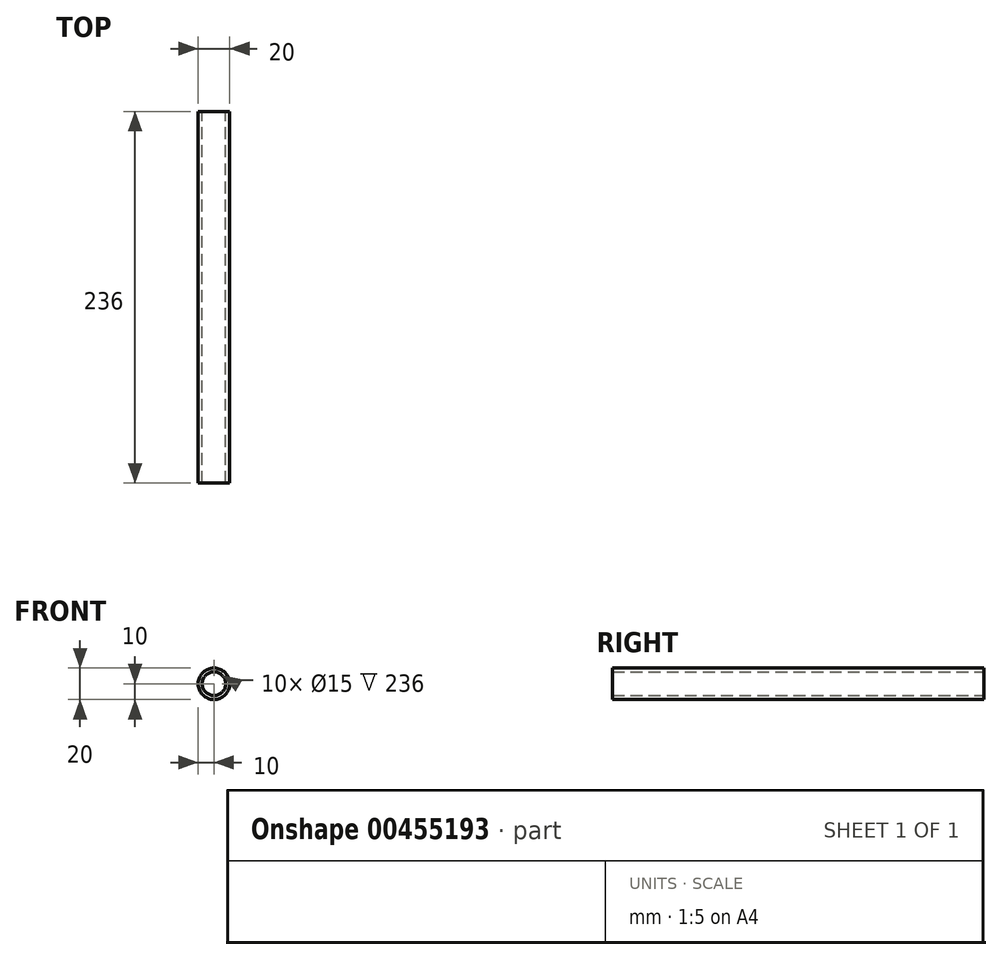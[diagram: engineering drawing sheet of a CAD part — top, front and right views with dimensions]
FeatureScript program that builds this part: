
annotation { "Feature Type Name" : "Feature", "Feature Type Description" : "" }
export const myFeature = defineFeature(function(context is Context, id is Id, definition is map)
    precondition{}
    {
        {
            var Q0;
            Q0=qCreatedBy(makeId("Front.planeOp"),FACE);
            var sketch = newSketch(context, id + "F0", { "sketchPlane" : qUnion([Q0])});
            skCircle(sketch, "E0", {"center": v(0, 0) * mm, "radius": 10 * mm});
            skCircle(sketch, "E1", {"center": v(0, 0) * mm, "radius": 7.5 * mm});
            skSolve(sketch);
        }
        {
            var Q0;
            Q0 = qSketchRegion(id + "F0", true);
            extrude(context, id + "F1", {"entities" : qUnion([Q0]), "depth" : 236 * mm});
        }
    });
